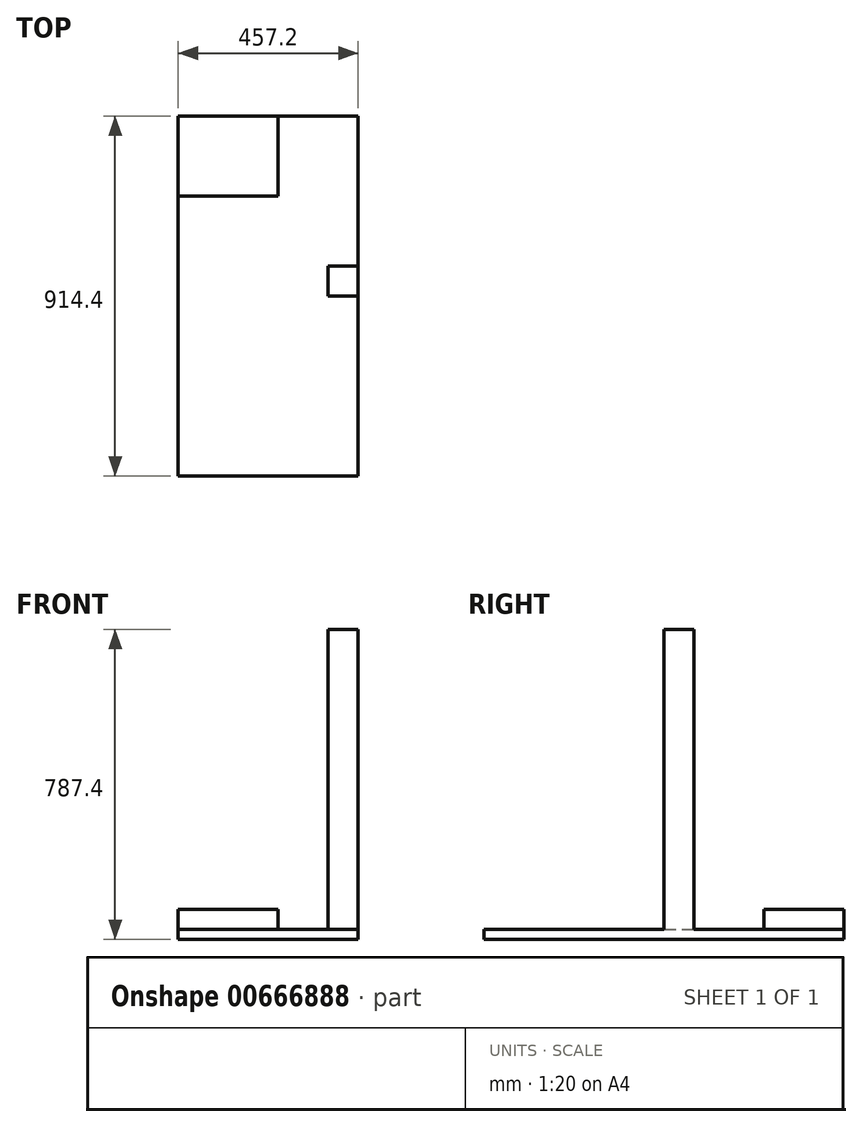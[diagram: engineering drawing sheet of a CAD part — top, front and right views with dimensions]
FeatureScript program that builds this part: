
annotation { "Feature Type Name" : "Feature", "Feature Type Description" : "" }
export const myFeature = defineFeature(function(context is Context, id is Id, definition is map)
    precondition{}
    {
        {
            var Q0;
            Q0=qCreatedBy(makeId("Top.planeOp"),FACE);
            var sketch = newSketch(context, id + "F0", { "sketchPlane" : qUnion([Q0])});
            skLineSegment(sketch, "E0.bottom", {"start": v(0, 0) * mm, "end": v(457.2, 0) * mm});
            skLineSegment(sketch, "E0.top", {"start": v(0, -914.4) * mm, "end": v(457.2, -914.4) * mm});
            skLineSegment(sketch, "E0.left", {"start": v(0, 0) * mm, "end": v(0, -914.4) * mm});
            skLineSegment(sketch, "E0.right", {"start": v(457.2, 0) * mm, "end": v(457.2, -914.4) * mm});
            skLineSegment(sketch, "E1.bottom", {"start": v(0, 0) * mm, "end": v(254, 0) * mm});
            skLineSegment(sketch, "E1.top", {"start": v(0, -203.2) * mm, "end": v(254, -203.2) * mm});
            skLineSegment(sketch, "E1.left", {"start": v(0, 0) * mm, "end": v(0, -203.2) * mm});
            skLineSegment(sketch, "E1.right", {"start": v(254, 0) * mm, "end": v(254, -203.2) * mm});
            skLineSegment(sketch, "E2.bottom", {"start": v(457.2, -457.2) * mm, "end": v(381, -457.2) * mm});
            skLineSegment(sketch, "E2.top", {"start": v(457.2, -381) * mm, "end": v(381, -381) * mm});
            skLineSegment(sketch, "E2.left", {"start": v(457.2, -457.2) * mm, "end": v(457.2, -381) * mm});
            skLineSegment(sketch, "E2.right", {"start": v(381, -457.2) * mm, "end": v(381, -381) * mm});
            skSolve(sketch);
        }
        {
            var Q0;
            {var subQ4=sQuery(id+"F0.wireOp",EDGE,"E1.top");Q0=makeQuery(id+"F0.imprint","IMPRINT",FACE,{"disambiguationData":[TD([[makeQuery(id+"F0.imprint","IMPRINT",EDGE,{"derivedFrom":subQ4}),1.0]])]});}
            var Q1;
            {var subQ1=sQuery(id+"F0.wireOp",EDGE,"E0.top");Q1=makeQuery(id+"F0.imprint","IMPRINT",FACE,{"disambiguationData":[TD([[makeQuery(id+"F0.imprint","IMPRINT",EDGE,{"derivedFrom":subQ1}),1.0]])]});}
            var Q2;
            {var subQ0=sQuery(id+"F0.wireOp",EDGE,"E2.bottom");Q2=makeQuery(id+"F0.imprint","IMPRINT",FACE,{"disambiguationData":[TD([[makeQuery(id+"F0.imprint","IMPRINT",EDGE,{"derivedFrom":subQ0}),-1.0]])]});}
            extrude(context, id + "F1", {"entities" : qUnion([Q0, Q1, Q2]), "oppositeDirection" : true, "depth" : 25.4 * mm, "offsetDistance" : 25.4 * mm});
        }
        {
            var Q0;
            {var subQ4=sQuery(id+"F0.wireOp",EDGE,"E1.top");Q0=makeQuery(id+"F0.imprint","IMPRINT",FACE,{"disambiguationData":[TD([[makeQuery(id+"F0.imprint","IMPRINT",EDGE,{"derivedFrom":subQ4}),1.0]])]});}
            extrude(context, id + "F2", {"entities" : qUnion([Q0]), "operationType" : NewBodyOperationType.ADD, "depth" : 50.8 * mm, "offsetDistance" : 25.4 * mm});
        }
        {
            var Q0;
            {var subQ0=sQuery(id+"F0.wireOp",EDGE,"E2.bottom");Q0=makeQuery(id+"F0.imprint","IMPRINT",FACE,{"disambiguationData":[TD([[makeQuery(id+"F0.imprint","IMPRINT",EDGE,{"derivedFrom":subQ0}),-1.0]])]});}
            extrude(context, id + "F3", {"entities" : qUnion([Q0]), "operationType" : NewBodyOperationType.ADD, "depth" : 762 * mm, "offsetDistance" : 25.4 * mm});
        }
    });
